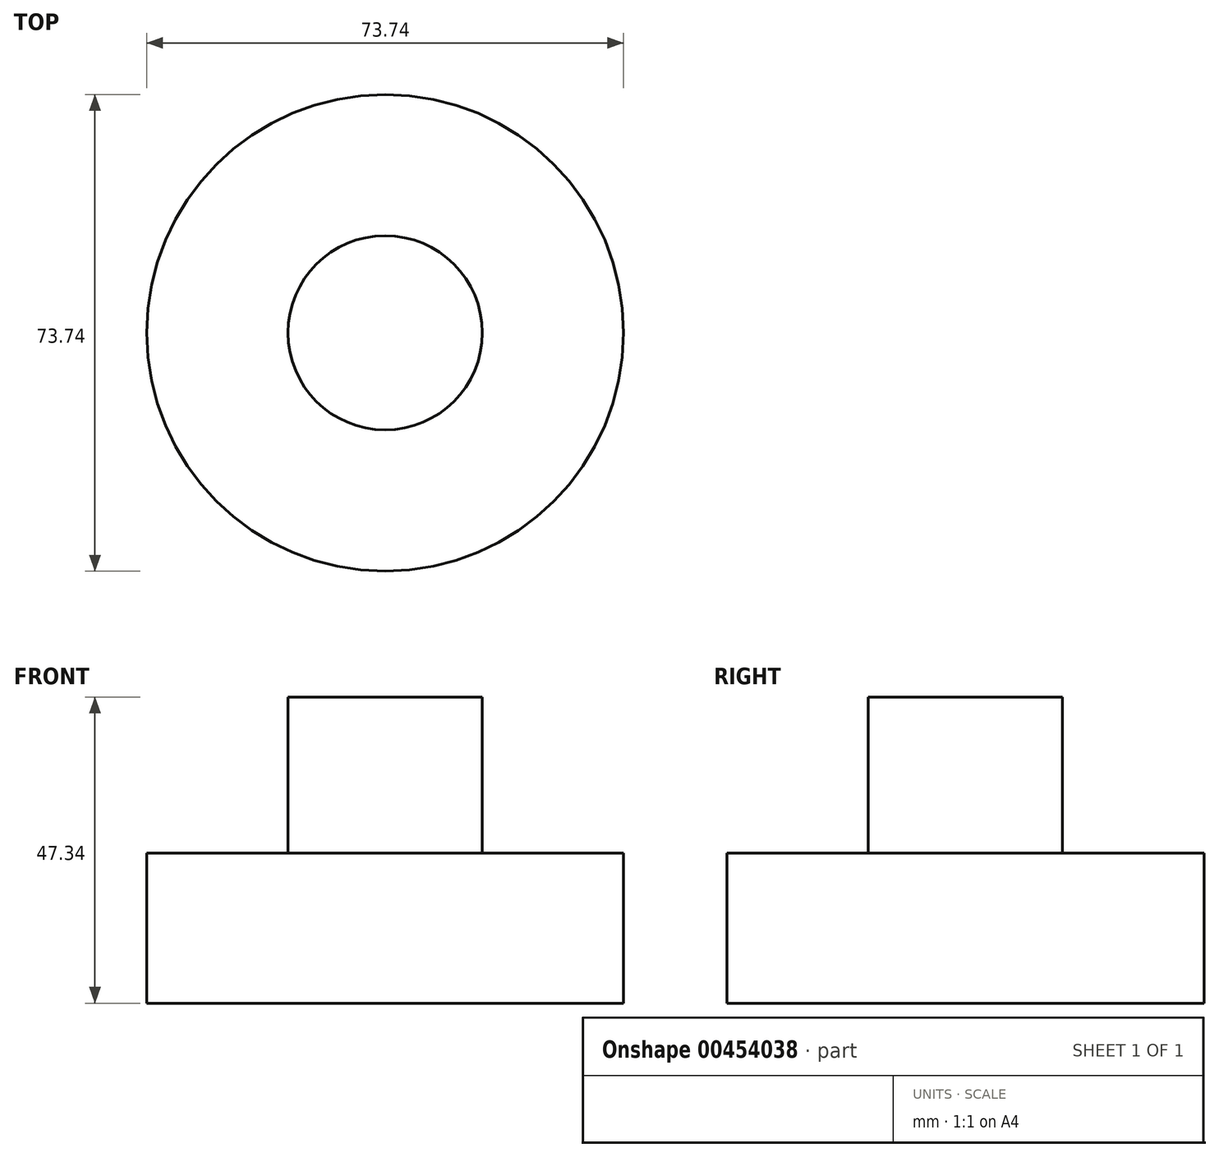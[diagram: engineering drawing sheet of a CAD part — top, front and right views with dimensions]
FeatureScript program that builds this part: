
annotation { "Feature Type Name" : "Feature", "Feature Type Description" : "" }
export const myFeature = defineFeature(function(context is Context, id is Id, definition is map)
    precondition{}
    {
        {
            var Q0;
            Q0=qCreatedBy(makeId("Front.planeOp"),FACE);
            var sketch = newSketch(context, id + "F0", { "sketchPlane" : qUnion([Q0])});
            skLineSegment(sketch, "E0.bottom", {"start": v(0, 0) * mm, "end": v(-36.87, 0) * mm});
            skLineSegment(sketch, "E0.top", {"start": v(0, 47.34) * mm, "end": v(-36.87, 47.34) * mm});
            skLineSegment(sketch, "E0.left", {"start": v(0, 0) * mm, "end": v(0, 47.34) * mm});
            skLineSegment(sketch, "E0.right", {"start": v(-36.87, 0) * mm, "end": v(-36.87, 47.34) * mm});
            skSolve(sketch);
        }
        {
            var Q0;
            Q0=makeQuery(id+"F0.imprint","IMPRINT",FACE,{"disambiguationData":[TD([[makeQuery(id+"F0.imprint","IMPRINT",EDGE,{"derivedFrom":sQuery(id+"F0.wireOp",EDGE,"E0.bottom")}),-1.0]])]});
            var Q1;
            Q1=sQuery(id+"F0.wireOp",EDGE,"E0.left");
            revolve(context, id + "F1", {"entities" : qUnion([Q0]), "axis" : qUnion([Q1]), "revolveType" : RevolveType.FULL});
        }
        {
            var Q0;
            Q0=qCreatedBy(makeId("Front.planeOp"),FACE);
            var sketch = newSketch(context, id + "F2", { "sketchPlane" : qUnion([Q0])});
            skLineSegment(sketch, "E1.bottom", {"start": v(-46.89, 52.8) * mm, "end": v(-15.02, 52.8) * mm});
            skLineSegment(sketch, "E1.top", {"start": v(-46.89, 23.22) * mm, "end": v(-15.02, 23.22) * mm});
            skLineSegment(sketch, "E1.left", {"start": v(-46.89, 52.8) * mm, "end": v(-46.89, 23.22) * mm});
            skLineSegment(sketch, "E1.right", {"start": v(-15.02, 52.8) * mm, "end": v(-15.02, 23.22) * mm});
            skLineSegment(sketch, "E2", {"start": v(0, 55.53) * mm, "end": v(0, 0) * mm});
            skSolve(sketch);
        }
        {
            var Q0;
            Q0 = qSketchRegion(id + "F2", true);
            var Q1;
            Q1=sQuery(id+"F2.wireOp",EDGE,"E2");
            revolve(context, id + "F3", {"operationType" : NewBodyOperationType.REMOVE, "entities" : qUnion([Q0]), "axis" : qUnion([Q1]), "revolveType" : RevolveType.FULL, "oppositeDirection" : true});
        }
    });
